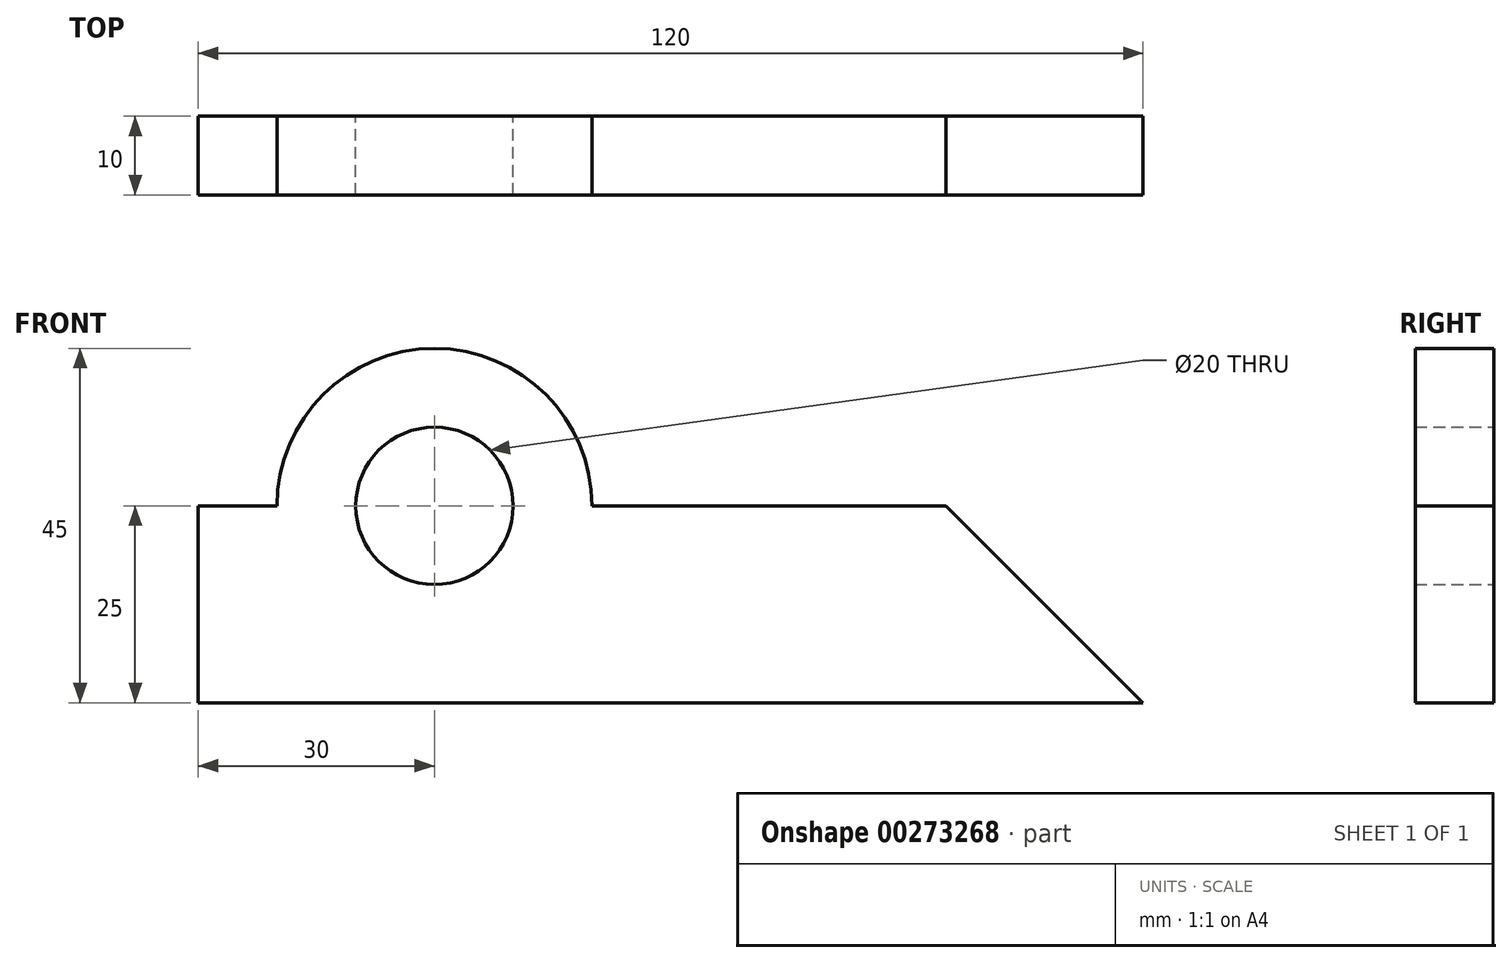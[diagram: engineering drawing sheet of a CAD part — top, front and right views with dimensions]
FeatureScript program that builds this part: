
annotation { "Feature Type Name" : "Feature", "Feature Type Description" : "" }
export const myFeature = defineFeature(function(context is Context, id is Id, definition is map)
    precondition{}
    {
        {
            var Q0;
            Q0=qCreatedBy(makeId("Front.planeOp"),FACE);
            var sketch = newSketch(context, id + "F0", { "sketchPlane" : qUnion([Q0])});
            skLineSegment(sketch, "E0", {"start": v(0, 0) * mm, "end": v(0, 25) * mm});
            skLineSegment(sketch, "E1", {"start": v(0, 25) * mm, "end": v(10, 25) * mm});
            skLineSegment(sketch, "E2", {"start": v(50, 25) * mm, "end": v(95, 25) * mm});
            skArc(sketch, "E3", {"start": v(50, 25) * mm, "mid": v(30, 45) * mm, "end": v(10, 25) * mm});
            skLineSegment(sketch, "E4", {"start": v(95, 25) * mm, "end": v(120, 0) * mm});
            skLineSegment(sketch, "E5", {"start": v(120, 0) * mm, "end": v(0, 0) * mm});
            skCircle(sketch, "E6", {"center": v(30, 25) * mm, "radius": 10 * mm});
            skSolve(sketch);
        }
        {
            var Q0;
            Q0=makeQuery(id+"F0.imprint","IMPRINT",FACE,{"disambiguationData":[TD([[makeQuery(id+"F0.imprint","IMPRINT",EDGE,{"derivedFrom":sQuery(id+"F0.wireOp",EDGE,"E0")}),-1.0]])]});
            extrude(context, id + "F1", {"entities" : qUnion([Q0]), "depth" : 10 * mm});
        }
    });
